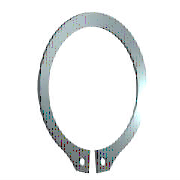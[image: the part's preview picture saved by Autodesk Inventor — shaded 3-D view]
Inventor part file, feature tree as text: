
AUTODESK INVENTOR PART (.ipt)
format: ipt  version: 2020 (Build 240168000, 168)  size: 155,136 bytes
history: native  units: mm (DEFAULTED — no unit token found)
features: extrude x1, other x1, plane x1
ambient origin geometry x8: Origin, YZ Plane, XZ Plane, XY Plane, X Axis, Y Axis, Z Axis, Center Point
bodies: Solid1 (feature_tree)
feature tree (3):
  extrude  "轴承体"  Depth=36.5mm
  other  "Work Axis1"
  plane  "Work Plane1"
